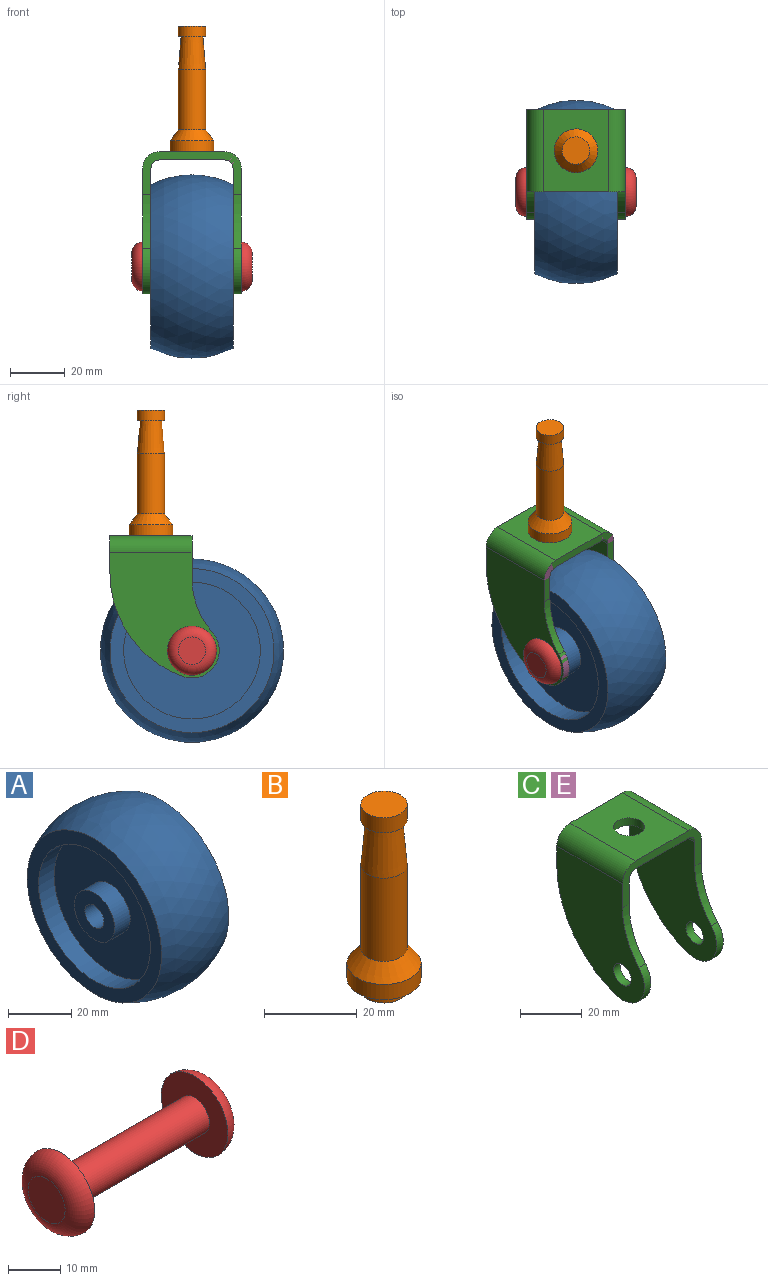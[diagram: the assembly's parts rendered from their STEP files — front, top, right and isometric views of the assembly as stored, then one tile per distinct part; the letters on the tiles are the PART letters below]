
ASSEMBLY  parts=5 mates=3
PART A: 12 faces, bbox 30x67.1x67.1 mm
  f0: plane 60x60mm, normal (-1,0,0), area 863.9mm2, adj f1,f11
  f1: cylinder r=25mm len=50mm, axis (-1,0,0), area 1099.6mm2, adj f0,f2
  f2: plane 50x50mm, normal (-1,0,0), area 1709mm2, adj f1,f3
  f3: cylinder r=9mm len=18mm, axis (-1,0,0), area 395.8mm2, adj f2,f4
  f4: plane 18x18mm, normal (-1,0,0), area 197.7mm2, adj f3,f5
  f5: cylinder r=4.25mm len=30mm, axis (-1,0,0), area 801.1mm2, adj f4,f6
  f6: plane 18x18mm, normal (1,0,0), area 197.7mm2, adj f5,f7
  f7: cylinder r=9mm len=18mm, axis (-1,0,0), area 395.8mm2, adj f6,f8
  f8: plane 50x50mm, normal (1,0,0), area 1709mm2, adj f7,f9
  f9: cylinder r=25mm len=50mm, axis (-1,0,0), area 1099.6mm2, adj f8,f10
  f10: plane 60x60mm, normal (1,0,0), area 863.9mm2, adj f9,f11
  f11: sphere r=33.54mm, area 6322.3mm2, adj f0,f10
PART B: 10 faces, bbox 16x16x49 mm
  f0: cylinder r=5mm len=10mm, axis (0,0,1), area 125.7mm2, adj f1,f9
  f1: plane 10x10mm, normal (0,0,-1), area 28.3mm2, adj f0,f2
  f2: cone r=4mm half-angle=4.8deg, axis (0,0,-1), area 340.5mm2, adj f1,f3
  f3: cylinder r=5mm len=22mm, axis (0,0,1), area 691.2mm2, adj f2,f4
  f4: cone r=8mm half-angle=36.9deg, axis (0,0,-1), area 204.2mm2, adj f3,f5
  f5: cylinder r=8mm len=16mm, axis (0,0,1), area 201.1mm2, adj f4,f6
  f6: plane 16x16mm, normal (0,0,-1), area 122.5mm2, adj f5,f7
  f7: cylinder r=5mm len=10mm, axis (0,0,1), area 94.2mm2, adj f6,f8
  f8: plane 10x10mm, normal (0,0,-1), area 78.5mm2, adj f7
  f9: plane 10x10mm, normal (0,0,1), area 78.5mm2, adj f0
PART C: 21 faces, bbox 36x40x52 mm
  f0: plane 36x15.54mm, normal (0,-1,0), area 171.7mm2, adj f1,f6,f9,f11,f12,f13,f14,f15
  f1: cylinder r=30mm len=19.84mm, axis (-1,0,0), area 65mm2, adj f0,f2,f11,f14
  f2: cylinder r=10mm len=16.61mm, axis (-1,0,0), area 79mm2, adj f1,f3,f11,f14
  f3: cylinder r=40mm len=37.71mm, axis (-1,0,0), area 147.7mm2, adj f2,f4,f11,f14
  f4: plane 36x13.72mm, normal (0,1,0), area 160.7mm2, adj f3,f8,f9,f11,f12,f13,f14,f15
  f5: cylinder r=4mm len=8mm, axis (-1,0,0), area 75.4mm2, adj f11,f14
  f6: cylinder r=30mm len=19.84mm, axis (-1,0,0), area 65mm2, adj f0,f7,f12,f15
  f7: cylinder r=10mm len=16.61mm, axis (-1,0,0), area 79mm2, adj f6,f8,f12,f15
  f8: cylinder r=40mm len=37.71mm, axis (-1,0,0), area 147.7mm2, adj f4,f7,f12,f15
  f9: plane 30x24mm, normal (0,0,1), area 641.5mm2, adj f0,f4,f18,f19,f20
  f10: cylinder r=4mm len=8mm, axis (-1,0,0), area 75.4mm2, adj f12,f15
  f11: plane 46x40mm, normal (1,0,0), area 1227.9mm2, adj f0,f1,f2,f3,f4,f5,f19
  f12: plane 46x40mm, normal (-1,0,0), area 1227.9mm2, adj f0,f4,f6,f7,f8,f10,f18
  f13: plane 30x24mm, normal (0,0,-1), area 641.5mm2, adj f0,f4,f16,f17,f20
  f14: plane 46x40mm, normal (-1,0,0), area 1227.9mm2, adj f0,f1,f2,f3,f4,f5,f17
  f15: plane 46x40mm, normal (1,0,0), area 1227.9mm2, adj f0,f4,f6,f7,f8,f10,f16
  f16: cylinder r=3mm len=30mm, axis (0,1,0), area 141.4mm2, adj f0,f4,f13,f15
  f17: cylinder r=3mm len=30mm, axis (0,-1,0), area 141.4mm2, adj f0,f4,f13,f14
  f18: cylinder r=6mm len=30mm, axis (0,-1,0), area 282.7mm2, adj f0,f4,f9,f12
  f19: cylinder r=6mm len=30mm, axis (0,1,0), area 282.7mm2, adj f0,f4,f9,f11
  f20: cylinder r=5mm len=10mm, axis (0,0,1), area 94.2mm2, adj f9,f13
PART D: 7 faces, bbox 44x19.5x19.5 mm
  f0: plane 10x10mm, normal (1,0,0), area 78.5mm2, adj f6
  f1: plane 18x18mm, normal (-1,0,0), area 204.2mm2, adj f2,f6
  f2: cylinder r=4mm len=36mm, axis (1,0,0), area 904.8mm2, adj f1,f4
  f3: plane 10x10mm, normal (-1,0,0), area 78.5mm2, adj f5
  f4: plane 18x18mm, normal (1,0,0), area 204.2mm2, adj f2,f5
  f5: torus R=5mm, axis (-1,0,0), area 297.9mm2, adj f3,f4
  f6: torus R=5mm, axis (1,0,0), area 297.9mm2, adj f0,f1
PART E: same geometry as C
PLACE A t=(47.37,-3.75,-42)mm
PLACE B t=(50.8,-15,22.11)mm
PLACE C at identity fixed
PLACE D t=(36,-30,-42)mm
PLACE E at identity
MATE revolute A.f1 <-> D.f2  axis (-1,0,0) through (18,-30,-42)mm
MATE revolute B.f0 <-> C.f20  axis (0,0,-1) through (18,-15,-3)mm
MATE revolute D.f2 <-> E.f2  axis (-1,0,0) through (36,-30,-42)mm
